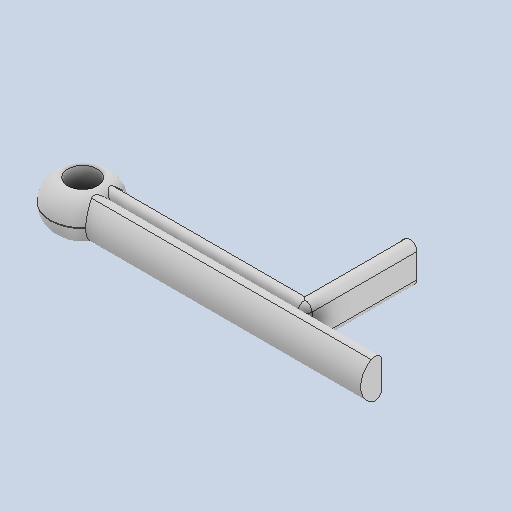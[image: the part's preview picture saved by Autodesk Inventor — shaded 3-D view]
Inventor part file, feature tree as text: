
AUTODESK INVENTOR PART (.ipt)
format: ipt  version: 2023 (Build 270158000, 158)  size: 331,264 bytes
history: native  units: in
note: dims shown in document units (in); Inventor stores cm internally (conversion verified against a paired STEP export)
features: fillet x5, extrude x2, sketch x1
ambient origin geometry x8: Origin, YZ Plane, XZ Plane, XY Plane, X Axis, Y Axis, Z Axis, Center Point
bodies: Solid1 (feature_tree)
feature tree (8):
  sketch  "Sketch5"  dims[d5=0.03in d6=0.06in d7=0.0in d10=0.03in d11=0.01in d16=0.01in d17=0.06in d18=0.0in d19=0.03in d20=0.01in d12=0.0in d13=0.0in d14=0.0in]
  extrude  "Extrusion1"  Depth=0.01in TaperAngle=0.0deg
  fillet  "Fillet1"  Radius=0.03in
  fillet  "Fillet2"  Radius=0.01in
  fillet  "Fillet5"  Radius=0.01in
  extrude  "Extrusion4"  Depth=0.01in TaperAngle=0.0deg
  fillet  "Fillet6"  Radius=0.03in
  fillet  "Fillet7"  Radius=0.01in
